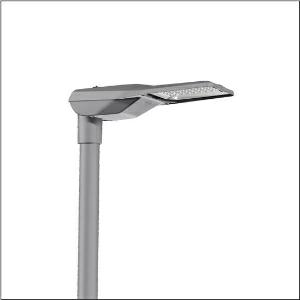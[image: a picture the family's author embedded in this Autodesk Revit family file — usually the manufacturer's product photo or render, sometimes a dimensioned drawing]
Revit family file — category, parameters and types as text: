
# Revit family: streetlight_sl_21_mini___pl52_5xe2h43s08gb_8da4
name_source: partatom
category: Lighting Fixtures
units: mm (PartAtom-declared; Revit-internal decimal feet)

## family parameters
Cut with Voids When Loaded = No
Host = Face
Light Source = No
Part Type = Normal
Room Calculation Point = No
Round Connector Dimension = Use Diameter
Shared = No

## types (1)
- --- (1 x LED, 6080 lm, 40.4 W, 4000K)
    Apparent Load = 40 VA
    CIE Flux Codes = 27 59 98 100 100
    Color Rendering = 70
    Color Temperature = 4000K
    Default Elevation = 1800 mm
    Description = Streetlight SL 21 mini, mast luminaire, primary light control with lens, of PMMA, primary optical cover: cover, of toughened safety glass, transparent, light distribution: PL52, light emission: direct distribution, primary light characteristic: asymmetric, installation type: side-entry, post-top, LED, High Power LED, rated luminous flux: 6.080lm, luminous efficacy: 151lm/W, light colour: 740, colour temperature: 4000K, control gear: D4i, control: overheat protection, constant luminous flux control, time-dependent luminous flux control, flexible luminous flux parameterisation, pre-setting: logarithmic dimming characteristic, mains connection: 220..240V, AC, 50/60Hz, start of lifetime: 40W, end of service life: 41W, reduction: 19W, luminaire housing, of diecast aluminium, powder-coated, SITECO metallic grey (DB 702S), corrosivity category C5 high according to DIN EN ISO 12944, please order mast flange separately, inclination adjustable: 0°, 5°, 10°, 15°, sealing non-destructively replaceable, multi-level sealing system, length: 628mm, width: 235mm, height: 110mm, mast flange for spigot size: 42mm (side-entry): 5XC10008XM4, 60/48mm (side-entry/post-top): 5XC10108XM2, 76/60mm (side-entry/post-top): 5XC10108XM1, mounting height: 4..8m, Smart Interface above, protection rating (complete): IP66, insulation class (complete): insulation class II (safety insulation), certification: CE, ENEC, ENEC+, VDE, impact resistance: IK10, permissible operating ambient temperature for outdoor applications: -40..+50°C, standard-compliant lighting for roads and squares, packaging unit: 1 piece

Light Distribution: PL52
    Height = 110 mm
    Lamp = 1 x LED
    Lamp Light Flux = 6080 lm
    Lamp Power = 40.4 W
    Lamp count = 1
    Length = 625 mm
    Luminous efficacy = 151 lm/W
    Manufacturer = Siteco
    ModVariant = No
    Model = 5XE2H43S08GB
    Mounting Place = Pole
    Mounting Type = Pole top
    Number of Poles = 1
    OnlyDefault = Yes
    Power Factor = 1
    Product Name = Streetlight SL 21 mini | PL52
    Product group = mast luminaire | pylon top
    ProductGroupID = 6100
    Protection Class = Protection class II
    Protection Degree = IP 66
    RLX_Detail_Level = 1
    RLX_Emergency_Light_Flux = 0 lm
    RLX_Emergency_Type = 0
    RLX_Emergency_Type_DB = No
    RlxData = <blob elided: 35737 chars, md5=c804f06d>
    Socket = socket
    Standby Power = 0 W
    System Light Flux = 6080 lm
    System Power = 40 W
    Type Comments = factory setting: luminous flux: 100 % | dim-lin: 254 | 812 mA
    Type Image = l_1003515.jpg
    URL = http://relux.com
    VarID = @adj_189187
    Voltage = 0 V
    Weight = 0.00 kg
    Width = 234 mm

## geometry (parser evidence)
native form markers: Blend x4, Sweep x9
no freeform markers — native parametric forms only
